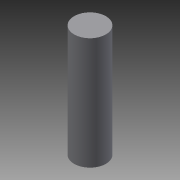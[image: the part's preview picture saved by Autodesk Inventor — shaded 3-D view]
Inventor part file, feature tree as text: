
AUTODESK INVENTOR PART (.ipt)
format: ipt  version: 2015 (Build 190159000, 159)  size: 65,024 bytes
history: native  units: mm
features: extrude x1, sketch x1
ambient origin geometry x8: Origin, YZ Plane, XZ Plane, XY Plane, X Axis, Y Axis, Z Axis, Center Point
bodies: Solid1 (feature_tree)
feature tree (2):
  extrude  "Extrusion1"  Depth=65.3mm TaperAngle=0.0deg
  sketch  "Sketch1"  dims[d0=18.5mm d1=65.3mm d2=0.0mm]
